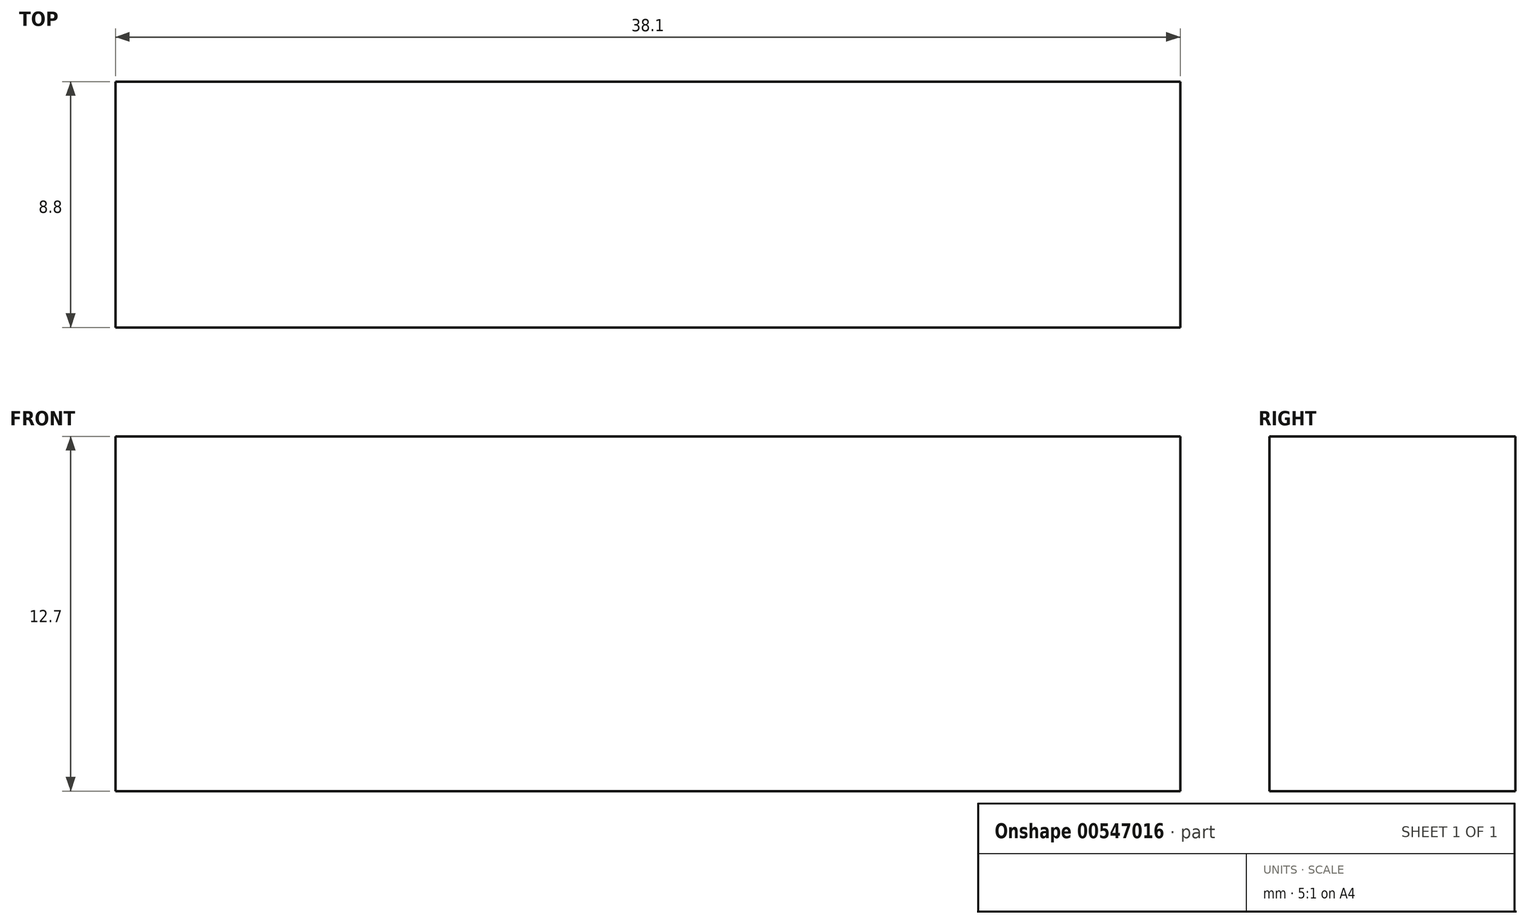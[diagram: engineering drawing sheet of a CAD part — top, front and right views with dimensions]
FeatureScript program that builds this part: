
annotation { "Feature Type Name" : "Feature", "Feature Type Description" : "" }
export const myFeature = defineFeature(function(context is Context, id is Id, definition is map)
    precondition{}
    {
        {
            var Q0;
            Q0=qCreatedBy(makeId("Front.planeOp"),FACE);
            var sketch = newSketch(context, id + "F0", { "sketchPlane" : qUnion([Q0])});
            skLineSegment(sketch, "E0", {"start": v(-67.5, 39.82) * mm, "end": v(-29.4, 39.82) * mm});
            skLineSegment(sketch, "E1", {"start": v(-29.4, 39.82) * mm, "end": v(-29.4, 27.12) * mm});
            skLineSegment(sketch, "E2", {"start": v(-29.4, 27.12) * mm, "end": v(-67.5, 27.12) * mm});
            skLineSegment(sketch, "E3", {"start": v(-67.5, 27.12) * mm, "end": v(-67.5, 39.82) * mm});
            skSolve(sketch);
        }
        {
            var Q0;
            Q0=makeQuery(id+"F0.imprint","IMPRINT",FACE,{"disambiguationData":[TD([[makeQuery(id+"F0.imprint","IMPRINT",EDGE,{"derivedFrom":sQuery(id+"F0.wireOp",EDGE,"E0")}),-1.0]])]});
            extrude(context, id + "F1", {"entities" : qUnion([Q0]), "depth" : 8.8 * mm, "offsetDistance" : 25.4 * mm});
        }
    });
